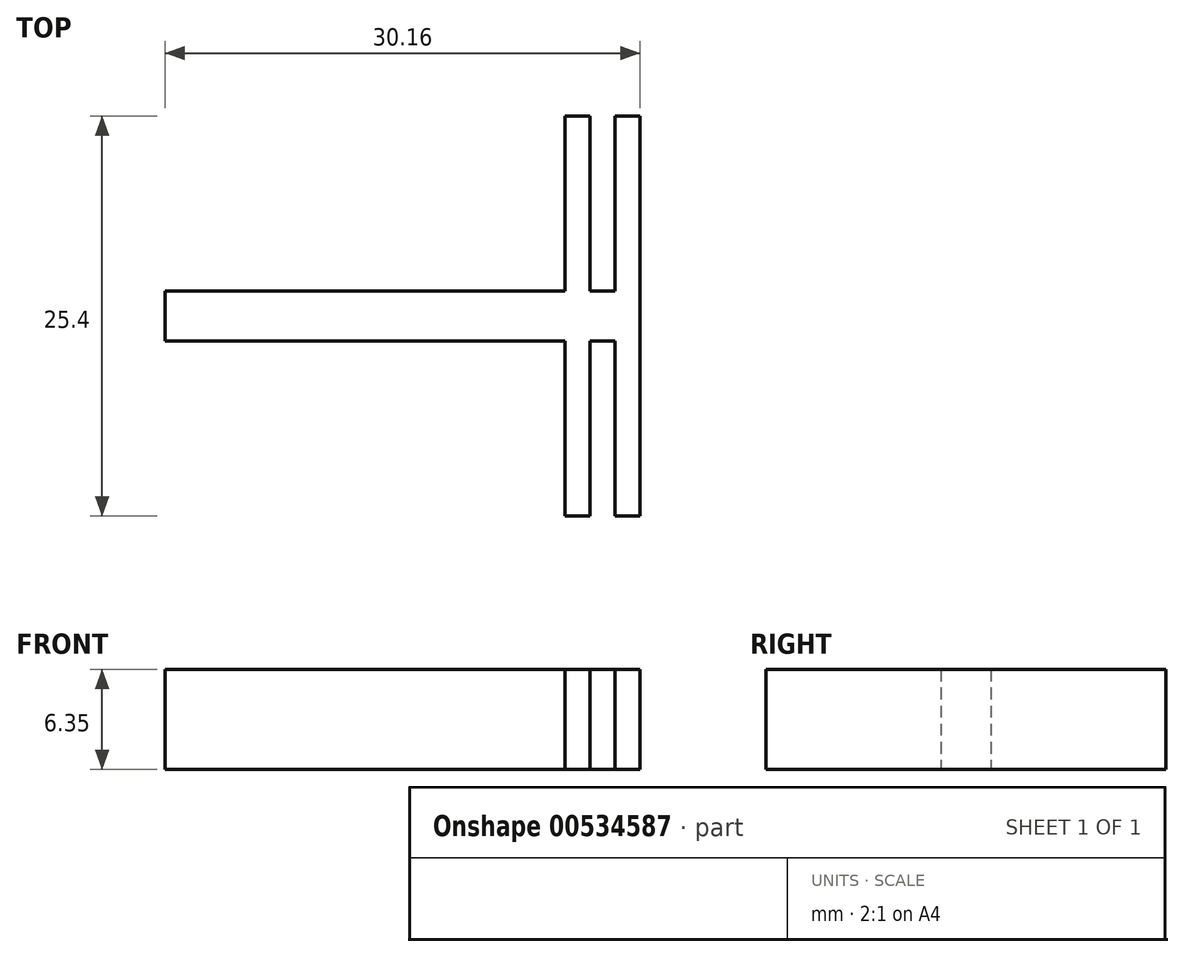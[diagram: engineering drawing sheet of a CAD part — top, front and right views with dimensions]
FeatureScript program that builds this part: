
annotation { "Feature Type Name" : "Feature", "Feature Type Description" : "" }
export const myFeature = defineFeature(function(context is Context, id is Id, definition is map)
    precondition{}
    {
        {
            var Q0;
            Q0=qCreatedBy(makeId("Top.planeOp"),FACE);
            var sketch = newSketch(context, id + "F0", { "sketchPlane" : qUnion([Q0])});
            skLineSegment(sketch, "E0.bottom", {"start": v(0, 0) * mm, "end": v(-1.59, 0) * mm});
            skLineSegment(sketch, "E0.top", {"start": v(0, -25.4) * mm, "end": v(-1.59, -25.4) * mm});
            skLineSegment(sketch, "E0.left", {"start": v(0, 0) * mm, "end": v(0, -25.4) * mm});
            skLineSegment(sketch, "E0.right", {"start": v(-1.59, 0) * mm, "end": v(-1.59, -25.4) * mm});
            skLineSegment(sketch, "E1", {"start": v(-1.59, 0) * mm, "end": v(-1.59, -11.11) * mm});
            skLineSegment(sketch, "E2.bottom", {"start": v(-1.59, -11.11) * mm, "end": v(-3.18, -11.11) * mm});
            skLineSegment(sketch, "E2.top", {"start": v(-1.59, -14.29) * mm, "end": v(-3.18, -14.29) * mm});
            skLineSegment(sketch, "E2.left", {"start": v(-1.59, -11.11) * mm, "end": v(-1.59, -14.29) * mm});
            skLineSegment(sketch, "E2.right", {"start": v(-3.18, -11.11) * mm, "end": v(-3.18, -14.29) * mm});
            skLineSegment(sketch, "E3", {"start": v(-1.59, 0) * mm, "end": v(-3.18, 0) * mm});
            skLineSegment(sketch, "E4.bottom", {"start": v(-3.18, 0) * mm, "end": v(-4.76, 0) * mm});
            skLineSegment(sketch, "E4.top", {"start": v(-3.17, -25.4) * mm, "end": v(-4.76, -25.4) * mm});
            skLineSegment(sketch, "E4.left", {"start": v(-3.18, 0) * mm, "end": v(-3.17, -25.4) * mm});
            skLineSegment(sketch, "E4.right", {"start": v(-4.76, 0) * mm, "end": v(-4.76, -25.4) * mm});
            skLineSegment(sketch, "E5", {"start": v(-3.18, -11.11) * mm, "end": v(-4.76, -11.11) * mm});
            skLineSegment(sketch, "E6.bottom", {"start": v(-4.76, -11.11) * mm, "end": v(-30.16, -11.11) * mm});
            skLineSegment(sketch, "E6.top", {"start": v(-4.76, -14.29) * mm, "end": v(-30.16, -14.29) * mm});
            skLineSegment(sketch, "E6.left", {"start": v(-4.76, -11.11) * mm, "end": v(-4.76, -14.29) * mm});
            skLineSegment(sketch, "E6.right", {"start": v(-30.16, -11.11) * mm, "end": v(-30.16, -14.29) * mm});
            skSolve(sketch);
        }
        {
            var Q0;
            Q0=makeQuery(id+"F0.imprint","IMPRINT",FACE,{"disambiguationData":[TD([[makeQuery(id+"F0.imprint","IMPRINT",EDGE,{"derivedFrom":sQuery(id+"F0.wireOp",EDGE,"E6.bottom")}),1.0]])]});
            var Q1;
            {var subQ0=sQuery(id+"F0.wireOp",EDGE,"E4.bottom");Q1=makeQuery(id+"F0.imprint","IMPRINT",FACE,{"disambiguationData":[TD([[makeQuery(id+"F0.imprint","IMPRINT",EDGE,{"derivedFrom":subQ0}),1.0]])]});}
            var Q2;
            {var subQ2=sQuery(id+"F0.wireOp",EDGE,"E4.top");Q2=makeQuery(id+"F0.imprint","IMPRINT",FACE,{"disambiguationData":[TD([[makeQuery(id+"F0.imprint","IMPRINT",EDGE,{"derivedFrom":subQ2}),-1.0]])]});}
            var Q3;
            {var subQ0=sQuery(id+"F0.wireOp",EDGE,"E2.bottom");Q3=makeQuery(id+"F0.imprint","IMPRINT",FACE,{"disambiguationData":[TD([[makeQuery(id+"F0.imprint","IMPRINT",EDGE,{"derivedFrom":subQ0}),1.0]])]});}
            var Q4;
            Q4=makeQuery(id+"F0.imprint","IMPRINT",FACE,{"disambiguationData":[TD([[makeQuery(id+"F0.imprint","IMPRINT",EDGE,{"derivedFrom":sQuery(id+"F0.wireOp",EDGE,"E0.bottom")}),1.0]])]});
            extrude(context, id + "F1", {"entities" : qUnion([Q0, Q1, Q2, Q3, Q4]), "depth" : 6.35 * mm, "offsetDistance" : 25.4 * mm});
        }
    });
